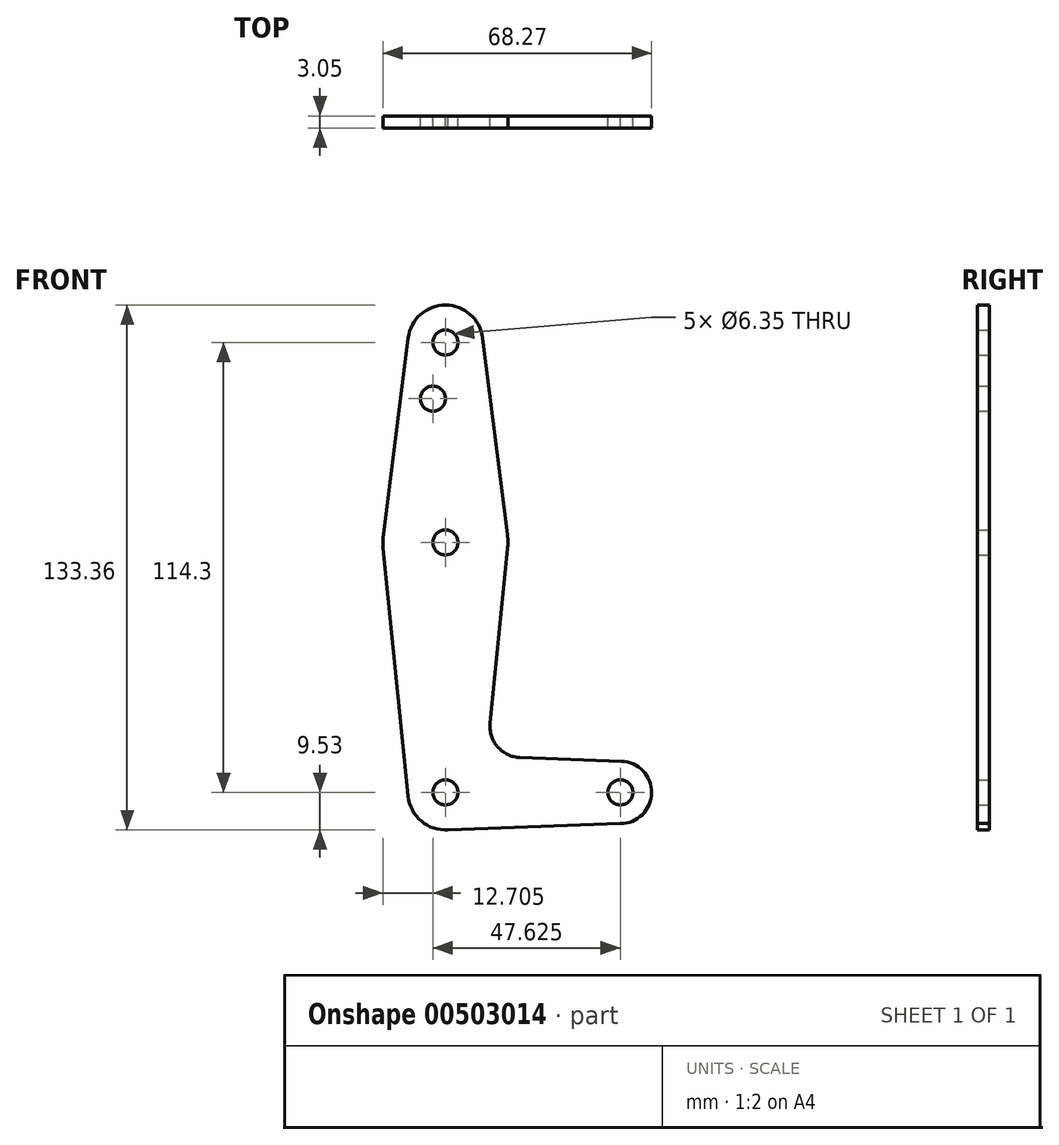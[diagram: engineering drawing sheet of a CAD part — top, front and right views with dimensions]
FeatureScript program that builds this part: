
annotation { "Feature Type Name" : "Feature", "Feature Type Description" : "" }
export const myFeature = defineFeature(function(context is Context, id is Id, definition is map)
    precondition{}
    {
        {
            var Q0;
            Q0=qCreatedBy(makeId("Front.planeOp"),FACE);
            var sketch = newSketch(context, id + "F0", { "sketchPlane" : qUnion([Q0])});
            skCircle(sketch, "E0", {"center": v(0, 114.3) * mm, "radius": 9.53 * mm});
            skCircle(sketch, "E1", {"center": v(0, 63.5) * mm, "radius": 15.88 * mm});
            skCircle(sketch, "E2", {"center": v(0, 0) * mm, "radius": 9.53 * mm});
            skLineSegment(sketch, "E3", {"start": v(0, 114.3) * mm, "end": v(44.45, 114.3) * mm, "construction": true});
            skLineSegment(sketch, "E4", {"start": v(44.45, 114.3) * mm, "end": v(44.45, 0) * mm, "construction": true});
            skLineSegment(sketch, "E5", {"start": v(0, 63.5) * mm, "end": v(0, 0) * mm, "construction": true});
            skLineSegment(sketch, "E6", {"start": v(0, 63.5) * mm, "end": v(0, 114.3) * mm, "construction": true});
            skCircle(sketch, "E7", {"center": v(44.45, 0) * mm, "radius": 7.94 * mm});
            skLineSegment(sketch, "E8", {"start": v(0, 0) * mm, "end": v(44.45, 0) * mm, "construction": true});
            skLineSegment(sketch, "E9", {"start": v(0, 0) * mm, "end": v(0, -9.53) * mm, "construction": true});
            skLineSegment(sketch, "E10", {"start": v(44.45, 0) * mm, "end": v(44.45, -7.94) * mm, "construction": true});
            skLineSegment(sketch, "E11", {"start": v(0, -9.52) * mm, "end": v(44.45, -7.94) * mm});
            skPoint(sketch, "E12.startSnap0", {"position": v(0, -4.76) * mm});
            skCircle(sketch, "E13", {"center": v(0, 114.3) * mm, "radius": 3.18 * mm});
            skCircle(sketch, "E14", {"center": v(0, 0) * mm, "radius": 3.18 * mm});
            skCircle(sketch, "E15", {"center": v(44.45, 0) * mm, "radius": 3.18 * mm});
            skCircle(sketch, "E16", {"center": v(0, 63.5) * mm, "radius": 3.18 * mm});
            skLineSegment(sketch, "E17", {"start": v(0, 63.5) * mm, "end": v(34.28, 63.5) * mm, "construction": true});
            skPoint(sketch, "E18.newPointB", {"position": v(0, 9.52) * mm});
            skCircle(sketch, "E19", {"center": v(-3.17, 100.03) * mm, "radius": 3.18 * mm});
            skLineSegment(sketch, "E20", {"start": v(-3.18, 100.03) * mm, "end": v(-21.88, 100.03) * mm, "construction": true});
            skLineSegment(sketch, "E21", {"start": v(0, 100.03) * mm, "end": v(-3.17, 100.03) * mm, "construction": true});
            skLineSegment(sketch, "E22", {"start": v(-9.45, 115.5) * mm, "end": v(-15.75, 65.48) * mm});
            skLineSegment(sketch, "E23", {"start": v(9.45, 115.5) * mm, "end": v(15.75, 65.48) * mm});
            skLineSegment(sketch, "E24", {"start": v(-15.8, 61.91) * mm, "end": v(-9.48, -0.95) * mm});
            skLineSegment(sketch, "E25", {"start": v(15.8, 61.91) * mm, "end": v(11.34, 17.6) * mm});
            skLineSegment(sketch, "E26", {"start": v(18.97, 8.85) * mm, "end": v(44.73, 7.93) * mm});
            skArc(sketch, "E27.filletArc", {"start": v(11.34, 17.6) * mm, "mid": v(13.26, 11.57) * mm, "end": v(18.97, 8.85) * mm});
            skSolve(sketch);
        }
        {
            var Q0;
            Q0 = qSketchRegion(id + "F0", true);
            extrude(context, id + "F1", {"entities" : qUnion([Q0]), "depth" : 3.05 * mm, "offsetDistance" : 25.4 * mm});
        }
    });
